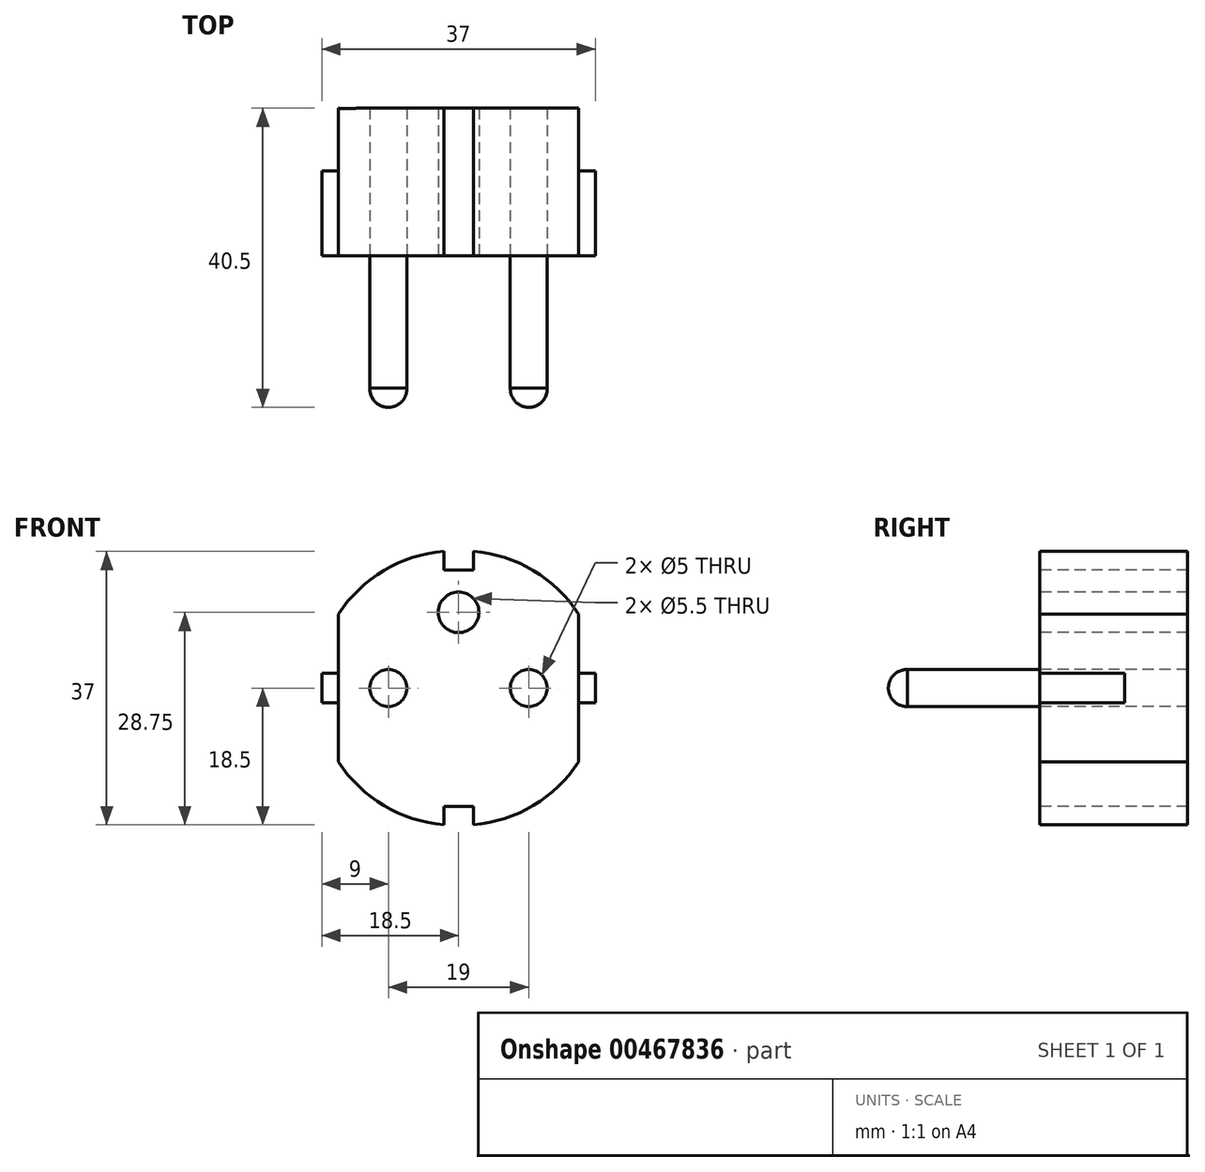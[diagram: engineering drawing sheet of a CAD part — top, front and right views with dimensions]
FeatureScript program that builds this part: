
annotation { "Feature Type Name" : "Feature", "Feature Type Description" : "" }
export const myFeature = defineFeature(function(context is Context, id is Id, definition is map)
    precondition{}
    {
        {
            var Q0;
            Q0=qCreatedBy(makeId("Front.planeOp"),FACE);
            var sketch = newSketch(context, id + "F0", { "sketchPlane" : qUnion([Q0])});
            skLineSegment(sketch, "E0.right", {"start": v(-16.25, 2) * mm, "end": v(-16.25, 10) * mm});
            skArc(sketch, "E1", {"start": v(-2, 18.5) * mm, "mid": v(-10.12, 15.91) * mm, "end": v(-16.25, 10) * mm});
            skArc(sketch, "E2.MirrorCS", {"start": v(2, 18.5) * mm, "mid": v(10.12, 15.91) * mm, "end": v(16.25, 10) * mm});
            skLineSegment(sketch, "E3", {"start": v(-18.5, 0) * mm, "end": v(-18.5, 2) * mm});
            skLineSegment(sketch, "E4", {"start": v(-18.5, 2) * mm, "end": v(-16.25, 2) * mm});
            skLineSegment(sketch, "E5.MirrorCS", {"start": v(18.5, 0) * mm, "end": v(18.5, 2) * mm});
            skLineSegment(sketch, "E6.MirrorCS", {"start": v(18.5, 2) * mm, "end": v(16.25, 2) * mm});
            skLineSegment(sketch, "E7.MirrorCS", {"start": v(16.25, 2) * mm, "end": v(16.25, 10) * mm});
            skLineSegment(sketch, "E8", {"start": v(-2, 18.5) * mm, "end": v(-2, 16) * mm});
            skLineSegment(sketch, "E9", {"start": v(-2, 16) * mm, "end": v(2, 16) * mm});
            skLineSegment(sketch, "E10", {"start": v(2, 16) * mm, "end": v(2, 18.5) * mm});
            skLineSegment(sketch, "E11.MirrorCS", {"start": v(2, -16) * mm, "end": v(2, -18.5) * mm});
            skLineSegment(sketch, "E12.MirrorCS", {"start": v(-2, -18.5) * mm, "end": v(-2, -16) * mm});
            skLineSegment(sketch, "E13.MirrorCS", {"start": v(-18.5, -2) * mm, "end": v(-16.25, -2) * mm});
            skLineSegment(sketch, "E14.MirrorCS", {"start": v(18.5, -2) * mm, "end": v(16.25, -2) * mm});
            skLineSegment(sketch, "E15.MirrorCS", {"start": v(2, -18.5) * mm, "end": v(0, -18.5) * mm, "construction": true});
            skLineSegment(sketch, "E16.MirrorCS", {"start": v(-18.5, 0) * mm, "end": v(-18.5, -2) * mm});
            skLineSegment(sketch, "E17.MirrorCS", {"start": v(18.5, 0) * mm, "end": v(18.5, -2) * mm});
            skLineSegment(sketch, "E18.MirrorCS", {"start": v(-2, -16) * mm, "end": v(2, -16) * mm});
            skLineSegment(sketch, "E19.MirrorCS", {"start": v(16.25, -2) * mm, "end": v(16.25, -10) * mm});
            skArc(sketch, "E20.MirrorCS", {"start": v(-2, -18.5) * mm, "mid": v(-10.12, -15.91) * mm, "end": v(-16.25, -10) * mm});
            skArc(sketch, "E21.MirrorCS", {"start": v(2, -18.5) * mm, "mid": v(10.12, -15.91) * mm, "end": v(16.25, -10) * mm});
            skLineSegment(sketch, "E22.MirrorCS", {"start": v(-16.25, -2) * mm, "end": v(-16.25, -10) * mm});
            skCircle(sketch, "E23", {"center": v(-9.5, 0) * mm, "radius": 2.5 * mm});
            skCircle(sketch, "E24.MirrorC", {"center": v(9.5, 0) * mm, "radius": 2.5 * mm});
            skCircle(sketch, "E25", {"center": v(0, 10.25) * mm, "radius": 2.75 * mm});
            skPoint(sketch, "E26.top.end.orphan", {"position": v(0, 18.5) * mm});
            skLineSegment(sketch, "E27", {"start": v(16.25, 2) * mm, "end": v(16.25, -2) * mm});
            skLineSegment(sketch, "E28", {"start": v(-16.25, 2) * mm, "end": v(-16.25, -2) * mm});
            skSolve(sketch);
        }
        {
            var Q0;
            Q0=makeQuery(id+"F0.imprint","IMPRINT",FACE,{"disambiguationData":[TD([[makeQuery(id+"F0.imprint","IMPRINT",EDGE,{"derivedFrom":sQuery(id+"F0.wireOp",EDGE,"E5.MirrorCS")}),1.0]])]});
            var Q1;
            Q1=makeQuery(id+"F0.imprint","IMPRINT",FACE,{"disambiguationData":[TD([[makeQuery(id+"F0.imprint","IMPRINT",EDGE,{"derivedFrom":sQuery(id+"F0.wireOp",EDGE,"E3")}),-1.0]])]});
            extrude(context, id + "F1", {"entities" : qUnion([Q0, Q1]), "oppositeDirection" : true, "depth" : 11.5 * mm});
        }
        {
            var Q0;
            Q0=makeQuery(id+"F0.imprint","IMPRINT",FACE,{"disambiguationData":[TD([[makeQuery(id+"F0.imprint","IMPRINT",EDGE,{"derivedFrom":sQuery(id+"F0.wireOp",EDGE,"E0.right")}),-1.0]])]});
            var Q1;
            Q1=makeQuery(id+"F0.imprint","IMPRINT",FACE,{"disambiguationData":[TD([[makeQuery(id+"F0.imprint","IMPRINT",EDGE,{"derivedFrom":sQuery(id+"F0.wireOp",EDGE,"E25")}),1.0]])]});
            var Q2;
            Q2=makeQuery(id+"F0.imprint","IMPRINT",FACE,{"disambiguationData":[TD([[makeQuery(id+"F0.imprint","IMPRINT",EDGE,{"derivedFrom":sQuery(id+"F0.wireOp",EDGE,"E24.MirrorC")}),-1.0]])]});
            var Q3;
            Q3=makeQuery(id+"F0.imprint","IMPRINT",FACE,{"disambiguationData":[TD([[makeQuery(id+"F0.imprint","IMPRINT",EDGE,{"derivedFrom":sQuery(id+"F0.wireOp",EDGE,"E23")}),1.0]])]});
            extrude(context, id + "F2", {"entities" : qUnion([Q0, Q1, Q2, Q3]), "oppositeDirection" : true, "depth" : 20 * mm});
        }
        {
            var Q0;
            Q0=makeQuery(id+"F0.imprint","IMPRINT",FACE,{"disambiguationData":[TD([[makeQuery(id+"F0.imprint","IMPRINT",EDGE,{"derivedFrom":sQuery(id+"F0.wireOp",EDGE,"E25")}),1.0]])]});
            extrude(context, id + "F3", {"entities" : qUnion([Q0]), "operationType" : NewBodyOperationType.REMOVE, "oppositeDirection" : true, "depth" : 20 * mm});
        }
        {
            var Q0;
            Q0=qCreatedBy(makeId("Top.planeOp"),FACE);
            var sketch = newSketch(context, id + "F4", { "sketchPlane" : qUnion([Q0])});
            skLineSegment(sketch, "E29", {"start": v(0, 22) * mm, "end": v(0, -42.78) * mm, "construction": true});
            skLineSegment(sketch, "E30.0", {"start": v(-9.5, 37.96) * mm, "end": v(-9.5, -20.5) * mm, "construction": true});
            skLineSegment(sketch, "E31.MirrorCS", {"start": v(9.5, 37.96) * mm, "end": v(9.5, -42.78) * mm, "construction": true});
            skArc(sketch, "E32", {"start": v(-9.5, -20.5) * mm, "mid": v(-7.7, -19.74) * mm, "end": v(-7, -17.91) * mm});
            skLineSegment(sketch, "E33", {"start": v(-14.9, 0) * mm, "end": v(-3.7, 0) * mm, "construction": true});
            skLineSegment(sketch, "E34", {"start": v(-7, -17.91) * mm, "end": v(-7, 0) * mm});
            skLineSegment(sketch, "E35", {"start": v(-9.5, -20.5) * mm, "end": v(-9.5, -42.78) * mm, "construction": true});
            skLineSegment(sketch, "E36.MirrorCS", {"start": v(7, -17.91) * mm, "end": v(7, 0) * mm});
            skArc(sketch, "E37.MirrorCS", {"start": v(9.5, -20.5) * mm, "mid": v(7.7, -19.74) * mm, "end": v(7, -17.91) * mm});
            skLineSegment(sketch, "E38", {"start": v(-9.5, -20.5) * mm, "end": v(-9.5, 0) * mm});
            skLineSegment(sketch, "E39", {"start": v(-9.5, 0) * mm, "end": v(-7, 0) * mm});
            skLineSegment(sketch, "E40", {"start": v(7, 0) * mm, "end": v(9.5, 0) * mm});
            skLineSegment(sketch, "E41", {"start": v(9.5, 0) * mm, "end": v(9.5, -20.5) * mm});
            skLineSegment(sketch, "E42.0", {"start": v(-16.2, 37.96) * mm, "end": v(-16.2, -20.5) * mm, "construction": true});
            skLineSegment(sketch, "E43.0", {"start": v(16.2, 37.96) * mm, "end": v(16.2, -42.78) * mm});
            skArc(sketch, "E44", {"start": v(16.2, 20.17) * mm, "mid": v(-0.01, 22) * mm, "end": v(-16.2, 19.98) * mm});
            skLineSegment(sketch, "E45", {"start": v(-16.2, 19.98) * mm, "end": v(16.2, 20.17) * mm});
            skSolve(sketch);
        }
        {
            var Q0;
            Q0=makeQuery(id+"F4.imprint","IMPRINT",FACE,{"disambiguationData":[TD([[makeQuery(id+"F4.imprint","IMPRINT",EDGE,{"derivedFrom":sQuery(id+"F4.wireOp",EDGE,"E32")}),1.0]])]});
            var Q1;
            Q1=sQuery(id+"F4.wireOp",EDGE,"E35");
            revolve(context, id + "F5", {"operationType" : NewBodyOperationType.ADD, "entities" : qUnion([Q0]), "axis" : qUnion([Q1]), "revolveType" : RevolveType.FULL});
        }
        {
            var Q0;
            Q0=makeQuery(id+"F2.opExtrude","SWEPT_BODY",BODY,{"disambiguationData":[OSD([sQuery(id+"F0.wireOp",EDGE,"E0.right"),sQuery(id+"F0.wireOp",EDGE,"E1"),sQuery(id+"F0.wireOp",EDGE,"E2.MirrorCS"),sQuery(id+"F0.wireOp",EDGE,"E7.MirrorCS"),sQuery(id+"F0.wireOp",EDGE,"E8"),sQuery(id+"F0.wireOp",EDGE,"E9"),sQuery(id+"F0.wireOp",EDGE,"E10"),sQuery(id+"F0.wireOp",EDGE,"E11.MirrorCS"),sQuery(id+"F0.wireOp",EDGE,"E12.MirrorCS"),sQuery(id+"F0.wireOp",EDGE,"E18.MirrorCS"),sQuery(id+"F0.wireOp",EDGE,"E19.MirrorCS"),sQuery(id+"F0.wireOp",EDGE,"E20.MirrorCS"),sQuery(id+"F0.wireOp",EDGE,"E21.MirrorCS"),sQuery(id+"F0.wireOp",EDGE,"E22.MirrorCS"),sQuery(id+"F0.wireOp",EDGE,"E27"),sQuery(id+"F0.wireOp",EDGE,"E28")])]});
            var Q1;
            Q1=qCreatedBy(makeId("Right.planeOp"),FACE);
            mirror(context, id + "F6", {"entities" : qUnion([Q0]), "mirrorPlane" : qUnion([Q1])});
        }
        {
            var Q0;
            Q0=makeQuery(id+"F2.opExtrude","CAP_FACE",FACE,{"disambiguationData":[OSD([sQuery(id+"F0.wireOp",EDGE,"E0.right"),sQuery(id+"F0.wireOp",EDGE,"E1"),sQuery(id+"F0.wireOp",EDGE,"E2.MirrorCS"),sQuery(id+"F0.wireOp",EDGE,"E7.MirrorCS"),sQuery(id+"F0.wireOp",EDGE,"E8"),sQuery(id+"F0.wireOp",EDGE,"E9"),sQuery(id+"F0.wireOp",EDGE,"E10"),sQuery(id+"F0.wireOp",EDGE,"E11.MirrorCS"),sQuery(id+"F0.wireOp",EDGE,"E12.MirrorCS"),sQuery(id+"F0.wireOp",EDGE,"E18.MirrorCS"),sQuery(id+"F0.wireOp",EDGE,"E19.MirrorCS"),sQuery(id+"F0.wireOp",EDGE,"E20.MirrorCS"),sQuery(id+"F0.wireOp",EDGE,"E21.MirrorCS"),sQuery(id+"F0.wireOp",EDGE,"E22.MirrorCS"),sQuery(id+"F0.wireOp",EDGE,"E27"),sQuery(id+"F0.wireOp",EDGE,"E28")])],"isStart":false});
            cPlane(context, id + "F7", {"entities" : qUnion([Q0]), "cplaneType" : CPlaneType.OFFSET, "offset" : 15 * mm, "width" : 150 * mm, "height" : 150 * mm});
        }
        {
            var Q0;
            Q0=makeQuery(id+"F4.imprint","IMPRINT",FACE,{"disambiguationData":[TD([[makeQuery(id+"F4.imprint","IMPRINT",EDGE,{"derivedFrom":sQuery(id+"F4.wireOp",EDGE,"E44")}),1.0]])]});
            extrude(context, id + "F8", {"entities" : qUnion([Q0]), "endBound" : BoundingType.SYMMETRIC, "depth" : 40 * mm});
        }
        {
            var Q0;
            Q0=makeQuery(id+"F8.opExtrude","SWEPT_FACE",FACE,{"disambiguationData":[OSD([sQuery(id+"F4.wireOp",EDGE,"E45")])]});
            extrude(context, id + "F9", {"entities" : qUnion([Q0]), "operationType" : NewBodyOperationType.REMOVE, "oppositeDirection" : true, "depth" : 25 * mm});
        }
    });
